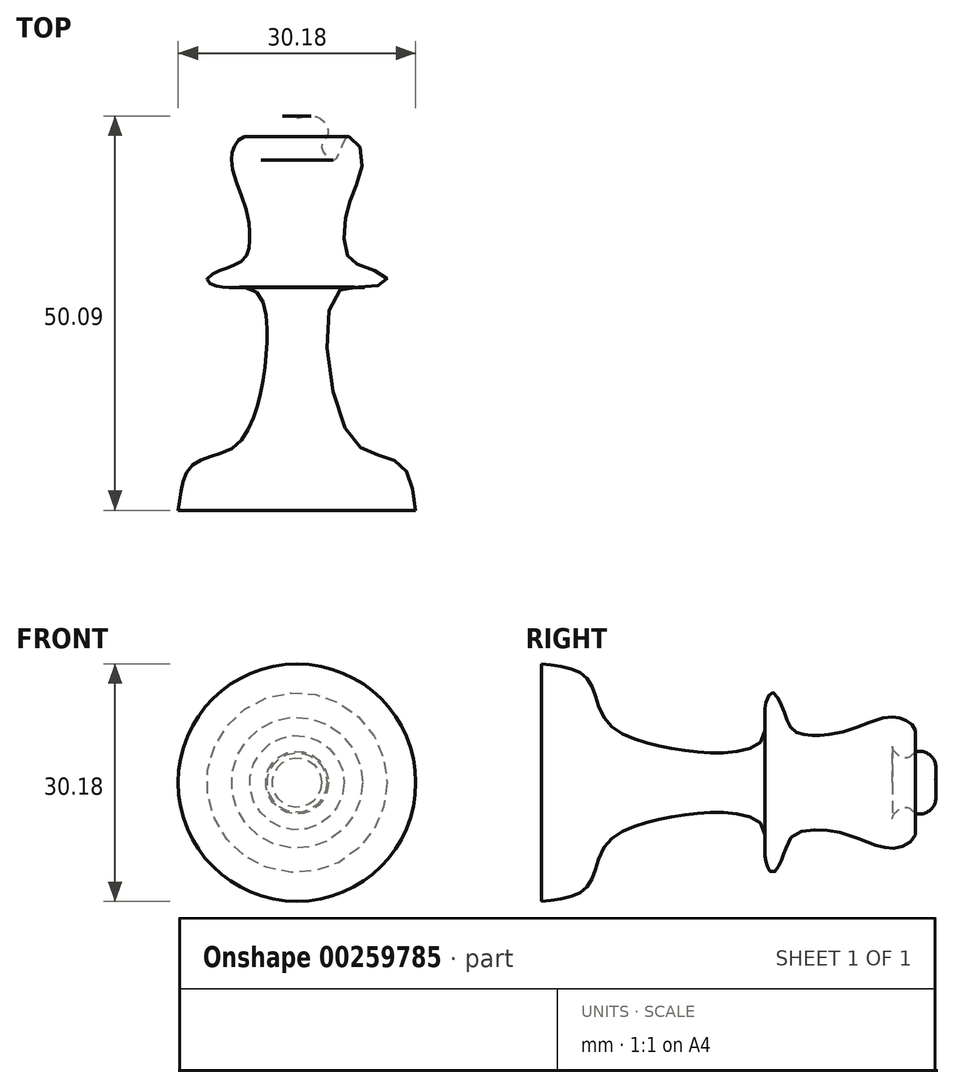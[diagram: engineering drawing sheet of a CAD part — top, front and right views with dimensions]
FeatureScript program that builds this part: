
annotation { "Feature Type Name" : "Feature", "Feature Type Description" : "" }
export const myFeature = defineFeature(function(context is Context, id is Id, definition is map)
    precondition{}
    {
        {
            var Q0;
            Q0=qCreatedBy(makeId("Top.planeOp"),FACE);
            var sketch = newSketch(context, id + "F0", { "sketchPlane" : qUnion([Q0])});
            skLineSegment(sketch, "E0", {"start": v(0, 0) * mm, "end": v(0, 49.82) * mm});
            skLineSegment(sketch, "E1", {"start": v(0, 0) * mm, "end": v(15.09, 0) * mm});
            skFitSpline(sketch, "E2", {"points": [v(0, 49.82) * mm, v(2.94, 49.82) * mm, v(3.95, 47.8) * mm, v(3.14, 46.17) * mm, v(4.76, 44.55) * mm, v(6.38, 47.39) * mm, v(8.2, 45.57) * mm, v(7.4, 40.9) * mm, v(6.18, 37.06) * mm, v(6.38, 32.4) * mm, v(8.4, 30.99) * mm, v(11.44, 29.37) * mm, v(9.21, 28.35) * mm, v(4.76, 27.34) * mm, v(6.38, 9.92) * mm, v(10.83, 6.89) * mm, v(13.87, 5.06) * mm, v(15.09, 0) * mm], "startDerivative": vector(61.53, 13.36) * mm, "endDerivative": vector(11.35, -82.37) * mm});
            skSolve(sketch);
        }
        {
            var Q0;
            Q0=makeQuery(id+"F0.imprint","IMPRINT",FACE,{"disambiguationData":[TD([[makeQuery(id+"F0.imprint","IMPRINT",EDGE,{"derivedFrom":sQuery(id+"F0.wireOp",EDGE,"E0")}),-1.0]])]});
            var Q1;
            Q1=sQuery(id+"F0.wireOp",EDGE,"E0");
            revolve(context, id + "F1", {"entities" : qUnion([Q0]), "axis" : qUnion([Q1]), "revolveType" : RevolveType.FULL});
        }
    });
